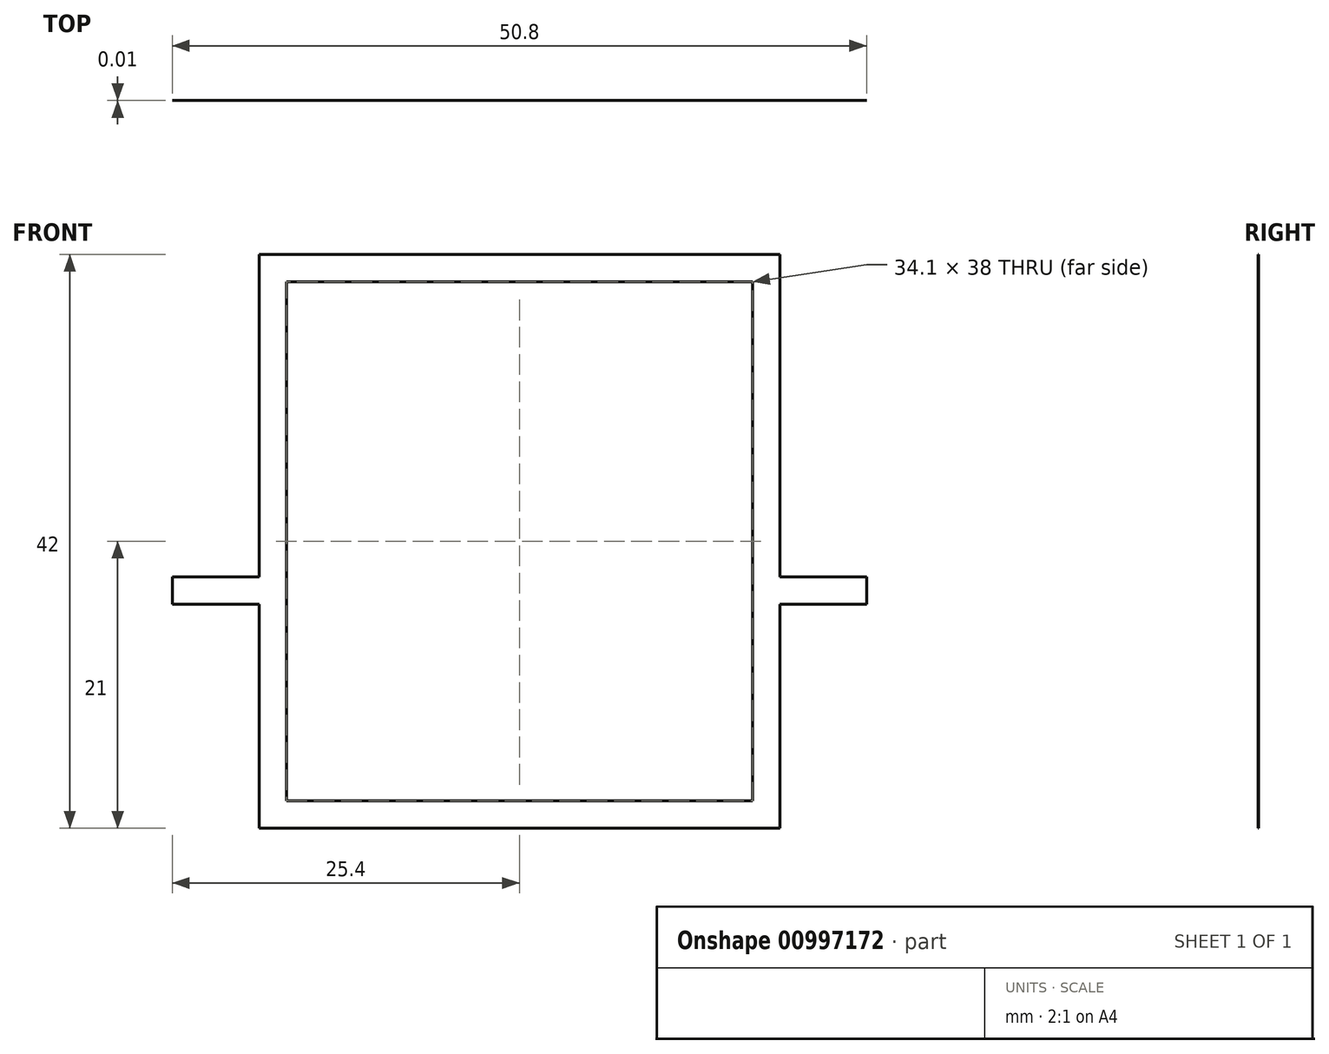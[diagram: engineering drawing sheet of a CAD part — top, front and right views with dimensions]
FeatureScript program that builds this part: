
annotation { "Feature Type Name" : "Feature", "Feature Type Description" : "" }
export const myFeature = defineFeature(function(context is Context, id is Id, definition is map)
    precondition{}
    {
        {
            var Q0;
            Q0=qCreatedBy(makeId("Front.planeOp"),FACE);
            var sketch = newSketch(context, id + "F0", { "sketchPlane" : qUnion([Q0])});
            skLineSegment(sketch, "E0", {"start": v(-25.4, 16.4) * mm, "end": v(-19.05, 16.4) * mm});
            skLineSegment(sketch, "E1", {"start": v(-19.05, 16.4) * mm, "end": v(-19.05, 0) * mm});
            skLineSegment(sketch, "E2", {"start": v(-19.05, 0) * mm, "end": v(0, 0) * mm});
            skLineSegment(sketch, "E3", {"start": v(0, 0) * mm, "end": v(0, 2) * mm});
            skLineSegment(sketch, "E4", {"start": v(0, 2) * mm, "end": v(-17.05, 2) * mm});
            skLineSegment(sketch, "E5", {"start": v(-17.05, 2) * mm, "end": v(-17.05, 40) * mm});
            skLineSegment(sketch, "E6", {"start": v(-17.05, 40) * mm, "end": v(0, 40) * mm});
            skLineSegment(sketch, "E7", {"start": v(0, 40) * mm, "end": v(0, 42) * mm});
            skLineSegment(sketch, "E8", {"start": v(0, 42) * mm, "end": v(-19.05, 42) * mm});
            skLineSegment(sketch, "E9", {"start": v(-19.05, 42) * mm, "end": v(-19.05, 18.4) * mm});
            skLineSegment(sketch, "E10", {"start": v(-19.05, 18.4) * mm, "end": v(-25.4, 18.4) * mm});
            skLineSegment(sketch, "E11", {"start": v(-25.4, 18.4) * mm, "end": v(-25.4, 16.4) * mm});
            skLineSegment(sketch, "E12", {"start": v(-17.05, 2) * mm, "end": v(-19.05, 2) * mm, "construction": true});
            skSolve(sketch);
        }
        {
            var Q0;
            Q0 = qSketchRegion(id + "F0", true);
            extrude(context, id + "F1", {"entities" : qUnion([Q0]), "depth" : 1 / 101.6 * mm, "offsetDistance" : 25 * mm});
        }
        {
            var Q0;
            Q0=makeQuery(id+"F1.opExtrude","SWEPT_BODY",BODY,{"disambiguationData":[OSD([sQuery(id+"F0.wireOp",EDGE,"E0"),sQuery(id+"F0.wireOp",EDGE,"E1"),sQuery(id+"F0.wireOp",EDGE,"E2"),sQuery(id+"F0.wireOp",EDGE,"E3"),sQuery(id+"F0.wireOp",EDGE,"E4"),sQuery(id+"F0.wireOp",EDGE,"E5"),sQuery(id+"F0.wireOp",EDGE,"E6"),sQuery(id+"F0.wireOp",EDGE,"E7"),sQuery(id+"F0.wireOp",EDGE,"E8"),sQuery(id+"F0.wireOp",EDGE,"E9"),sQuery(id+"F0.wireOp",EDGE,"E10"),sQuery(id+"F0.wireOp",EDGE,"E11")])]});
            var Q1;
            Q1=qCreatedBy(makeId("Right.planeOp"),FACE);
            mirror(context, id + "F2", {"operationType" : NewBodyOperationType.ADD, "entities" : qUnion([Q0]), "mirrorPlane" : qUnion([Q1])});
        }
    });
